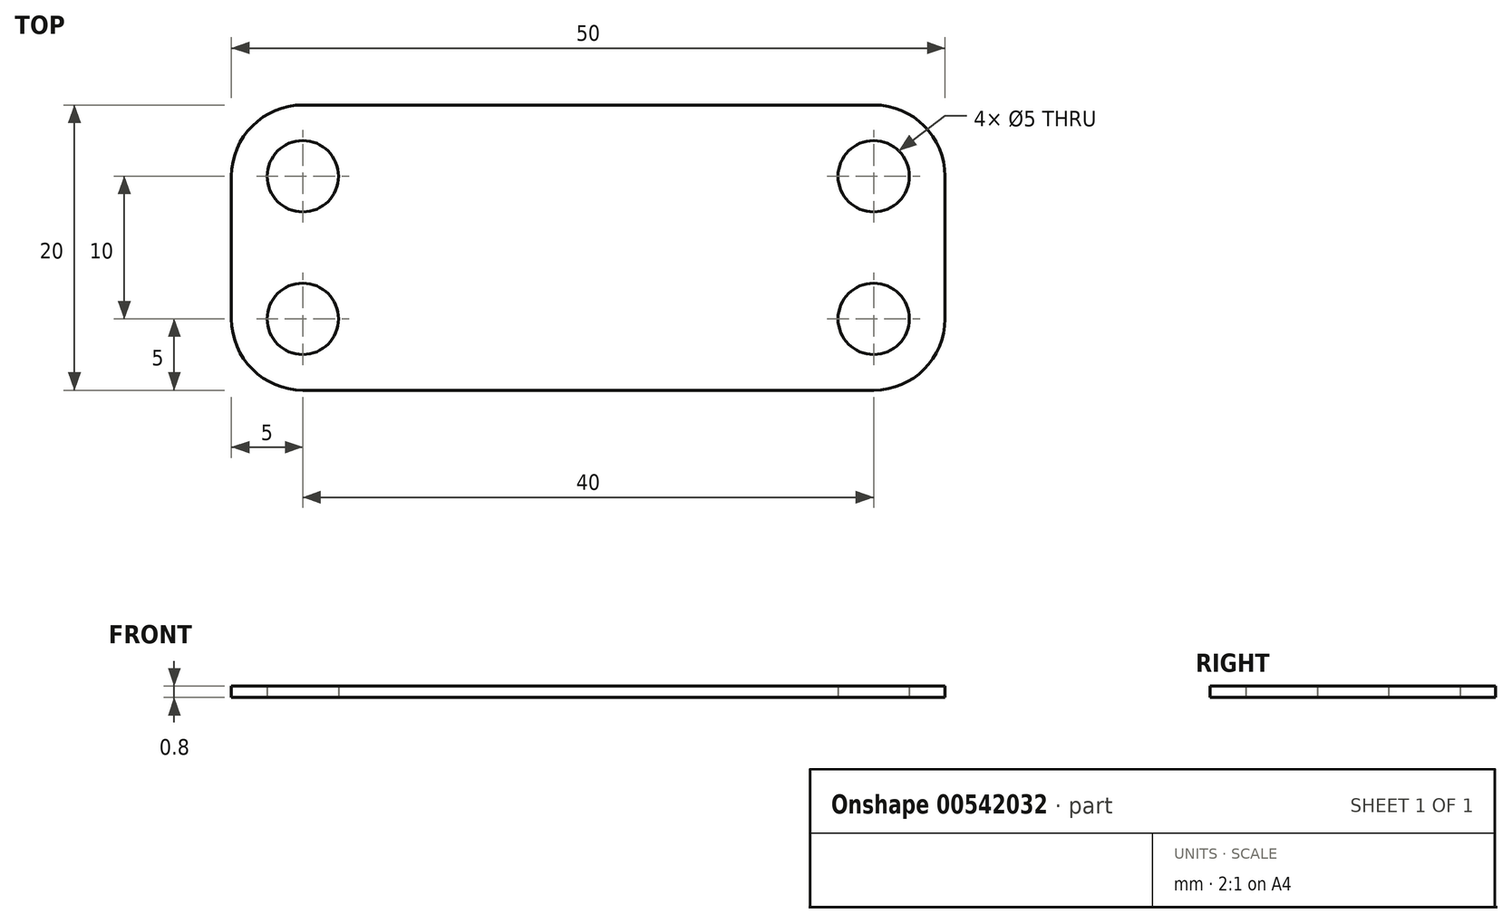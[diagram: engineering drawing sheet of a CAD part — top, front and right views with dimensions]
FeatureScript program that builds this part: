
annotation { "Feature Type Name" : "Feature", "Feature Type Description" : "" }
export const myFeature = defineFeature(function(context is Context, id is Id, definition is map)
    precondition{}
    {
        {
            var Q0;
            Q0=qCreatedBy(makeId("Top.planeOp"),FACE);
            var sketch = newSketch(context, id + "F0", { "sketchPlane" : qUnion([Q0])});
            skLineSegment(sketch, "E0.bottom", {"start": v(-45, 20) * mm, "end": v(-5, 20) * mm});
            skLineSegment(sketch, "E0.top", {"start": v(-45, 0) * mm, "end": v(-5, 0) * mm});
            skLineSegment(sketch, "E0.left", {"start": v(-50, 15) * mm, "end": v(-50, 5) * mm});
            skLineSegment(sketch, "E0.right", {"start": v(0, 15) * mm, "end": v(0, 5) * mm});
            skPoint(sketch, "E1.visualSharp", {"position": v(-50, 20) * mm});
            skArc(sketch, "E1.filletArc", {"start": v(-45, 20) * mm, "mid": v(-48.54, 18.54) * mm, "end": v(-50, 15) * mm});
            skPoint(sketch, "E2.visualSharp", {"position": v(-50, 0) * mm});
            skArc(sketch, "E2.filletArc", {"start": v(-50, 5) * mm, "mid": v(-48.54, 1.46) * mm, "end": v(-45, 0) * mm});
            skPoint(sketch, "E3.visualSharp", {"position": v(0, 20) * mm});
            skArc(sketch, "E3.filletArc", {"start": v(0, 15) * mm, "mid": v(-1.46, 18.54) * mm, "end": v(-5, 20) * mm});
            skPoint(sketch, "E4.visualSharp", {"position": v(0, 0) * mm});
            skArc(sketch, "E4.filletArc", {"start": v(-5, 0) * mm, "mid": v(-1.46, 1.46) * mm, "end": v(0, 5) * mm});
            skLineSegment(sketch, "E5.0", {"start": v(-45, 15) * mm, "end": v(-5, 15) * mm, "construction": true});
            skLineSegment(sketch, "E5.1", {"start": v(-45, 15) * mm, "end": v(-45, 5) * mm, "construction": true});
            skLineSegment(sketch, "E5.2", {"start": v(-45, 5) * mm, "end": v(-5, 5) * mm, "construction": true});
            skLineSegment(sketch, "E5.3", {"start": v(-5, 15) * mm, "end": v(-5, 5) * mm, "construction": true});
            skSolve(sketch);
        }
        {
            var Q0;
            Q0 = qSketchRegion(id + "F0", true);
            extrude(context, id + "F1", {"entities" : qUnion([Q0]), "depth" : 0.8 * mm, "offsetDistance" : 25 * mm});
        }
        {
            var Q0;
            Q0=sQuery(id+"F0.wireOp",VERTEX,"E1.filletArc.center");
            var Q1;
            Q1=sQuery(id+"F0.wireOp",VERTEX,"E3.filletArc.center");
            var Q2;
            Q2=sQuery(id+"F0.wireOp",VERTEX,"E5.3.end");
            var Q3;
            Q3=sQuery(id+"F0.wireOp",VERTEX,"E2.filletArc.center");
            var Q4;
            Q4=makeQuery(id+"F1.opExtrude","SWEPT_BODY",BODY,{"disambiguationData":[OSD([sQuery(id+"F0.wireOp",EDGE,"E0.bottom"),sQuery(id+"F0.wireOp",EDGE,"E0.top"),sQuery(id+"F0.wireOp",EDGE,"E0.left"),sQuery(id+"F0.wireOp",EDGE,"E0.right"),sQuery(id+"F0.wireOp",EDGE,"E1.filletArc"),sQuery(id+"F0.wireOp",EDGE,"E2.filletArc"),sQuery(id+"F0.wireOp",EDGE,"E3.filletArc"),sQuery(id+"F0.wireOp",EDGE,"E4.filletArc")])]});
            hole(context, id + "F2", {"style" : HoleStyle.SIMPLE, "endStyle" : HoleEndStyle.THROUGH, "oppositeDirection" : true, "holeDiameter" : 5 * mm, "isTappedThrough" : true, "tappedDepth" : 12 * mm, "tapClearance" : 3, "locations" : qUnion([Q0, Q1, Q2, Q3]), "scope" : qUnion([Q4])});
        }
    });
